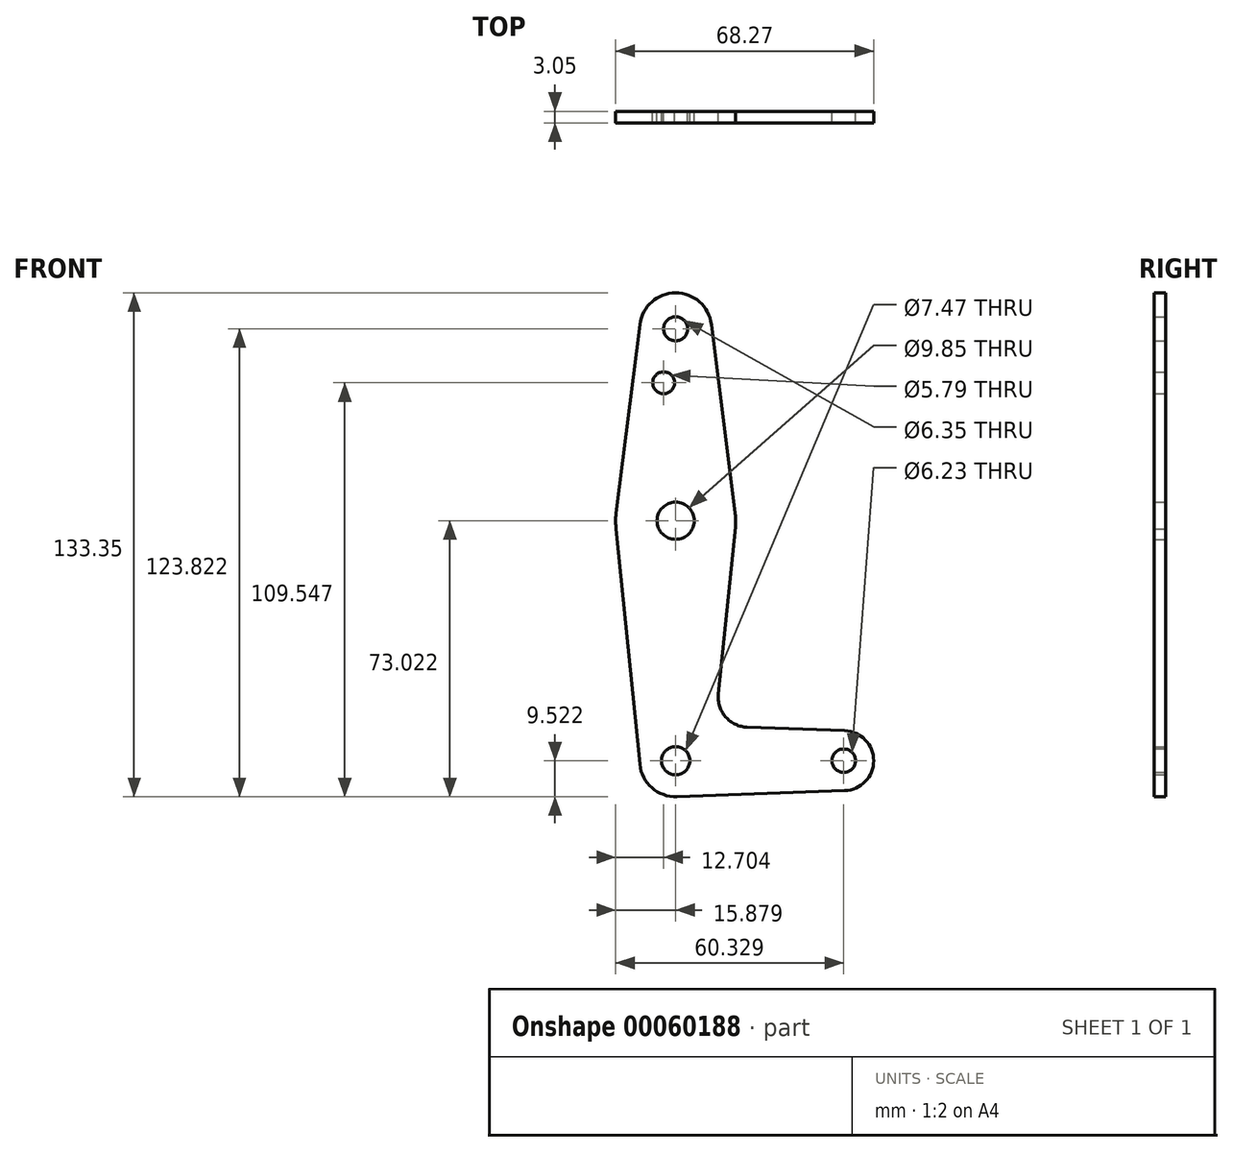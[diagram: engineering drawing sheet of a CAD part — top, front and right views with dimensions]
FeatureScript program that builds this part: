
annotation { "Feature Type Name" : "Feature", "Feature Type Description" : "" }
export const myFeature = defineFeature(function(context is Context, id is Id, definition is map)
    precondition{}
    {
        {
            var Q0;
            Q0=qCreatedBy(makeId("Front.planeOp"),FACE);
            var sketch = newSketch(context, id + "F0", { "sketchPlane" : qUnion([Q0])});
            skLineSegment(sketch, "E0", {"start": v(-32.87, 68.1) * mm, "end": v(-32.87, -46.2) * mm, "construction": true});
            skLineSegment(sketch, "E1", {"start": v(-32.87, -46.2) * mm, "end": v(11.58, -46.2) * mm, "construction": true});
            skCircle(sketch, "E2", {"center": v(-32.87, 68.1) * mm, "radius": 9.53 * mm});
            skCircle(sketch, "E3", {"center": v(-32.87, -46.2) * mm, "radius": 9.53 * mm});
            skCircle(sketch, "E4", {"center": v(11.58, -46.2) * mm, "radius": 7.94 * mm});
            skCircle(sketch, "E5", {"center": v(-32.87, 17.3) * mm, "radius": 15.88 * mm});
            skLineSegment(sketch, "E6", {"start": v(-23.42, 69.28) * mm, "end": v(-17.12, 19.28) * mm});
            skLineSegment(sketch, "E7", {"start": v(-42.32, 69.28) * mm, "end": v(-48.62, 19.28) * mm});
            skLineSegment(sketch, "E8", {"start": v(-48.6, 15.13) * mm, "end": v(-42.35, -47.16) * mm});
            skLineSegment(sketch, "E9", {"start": v(-32.53, -55.73) * mm, "end": v(11.86, -54.14) * mm});
            skLineSegment(sketch, "E10", {"start": v(11.86, -38.28) * mm, "end": v(-32.87, -36.68) * mm});
            skLineSegment(sketch, "E11", {"start": v(-23.35, -46.2) * mm, "end": v(-17.08, 15.7) * mm});
            skCircle(sketch, "E12", {"center": v(-32.87, 68.1) * mm, "radius": 3.18 * mm});
            skCircle(sketch, "E13", {"center": v(-32.87, 17.3) * mm, "radius": 4.92 * mm});
            skCircle(sketch, "E14", {"center": v(-32.87, -46.2) * mm, "radius": 3.74 * mm});
            skCircle(sketch, "E15", {"center": v(11.58, -46.2) * mm, "radius": 3.12 * mm});
            skPoint(sketch, "E16", {"position": v(-36.05, 53.82) * mm});
            skCircle(sketch, "E17", {"center": v(-36.05, 53.82) * mm, "radius": 2.9 * mm});
            skArc(sketch, "E18", {"start": v(-21.56, -28.6) * mm, "mid": v(-19.65, -34.63) * mm, "end": v(-13.94, -37.35) * mm});
            skSolve(sketch);
        }
        {
            var Q0;
            Q0=makeQuery(id+"F0.imprint","IMPRINT",FACE,{"disambiguationData":[TD([[makeQuery(id+"F0.imprint","IMPRINT",EDGE,{"derivedFrom":sQuery(id+"F0.wireOp",EDGE,"E12")}),-1.0]])]});
            var Q1;
            {var subQ1=sQuery(id+"F0.wireOp",EDGE,"E6");Q1=makeQuery(id+"F0.imprint","IMPRINT",FACE,{"disambiguationData":[TD([[makeQuery(id+"F0.imprint","IMPRINT",EDGE,{"derivedFrom":subQ1}),-1.0]])]});}
            var Q2;
            Q2=makeQuery(id+"F0.imprint","IMPRINT",FACE,{"disambiguationData":[TD([[makeQuery(id+"F0.imprint","IMPRINT",EDGE,{"derivedFrom":sQuery(id+"F0.wireOp",EDGE,"E13")}),-1.0]])]});
            var Q3;
            {var subQ0=sQuery(id+"F0.wireOp",EDGE,"E8");Q3=makeQuery(id+"F0.imprint","IMPRINT",FACE,{"disambiguationData":[TD([[makeQuery(id+"F0.imprint","IMPRINT",EDGE,{"derivedFrom":subQ0}),1.0]])]});}
            var Q4;
            Q4=makeQuery(id+"F0.imprint","IMPRINT",FACE,{"disambiguationData":[TD([[makeQuery(id+"F0.imprint","IMPRINT",EDGE,{"derivedFrom":sQuery(id+"F0.wireOp",EDGE,"E14")}),-1.0]])]});
            var Q5;
            {var subQ0=sQuery(id+"F0.wireOp",EDGE,"E11");var subQ1=sQuery(id+"F0.wireOp",EDGE,"E3");var subQ2=makeQuery(id+"F0.imprint","INTERSECT",VERTEX,{"derivedFrom":[subQ1,subQ0]});Q5=makeQuery(id+"F0.imprint","IMPRINT",FACE,{"disambiguationData":[TD([[makeQuery(id+"F0.imprint","IMPRINT",EDGE,{"disambiguationData":[TD([[subQ2,-1.0]])],"derivedFrom":subQ1}),-1.0]])]});}
            var Q6;
            {var subQ0=sQuery(id+"F0.wireOp",EDGE,"E18");Q6=makeQuery(id+"F0.imprint","IMPRINT",FACE,{"disambiguationData":[TD([[makeQuery(id+"F0.imprint","IMPRINT",EDGE,{"derivedFrom":subQ0}),-1.0]])]});}
            var Q7;
            {var subQ4=sQuery(id+"F0.wireOp",EDGE,"E9");Q7=makeQuery(id+"F0.imprint","IMPRINT",FACE,{"disambiguationData":[TD([[makeQuery(id+"F0.imprint","IMPRINT",EDGE,{"derivedFrom":subQ4}),1.0]])]});}
            var Q8;
            Q8=makeQuery(id+"F0.imprint","IMPRINT",FACE,{"disambiguationData":[TD([[makeQuery(id+"F0.imprint","IMPRINT",EDGE,{"derivedFrom":sQuery(id+"F0.wireOp",EDGE,"E15")}),-1.0]])]});
            extrude(context, id + "F1", {"entities" : qUnion([Q0, Q1, Q2, Q3, Q4, Q5, Q6, Q7, Q8]), "depth" : 3.05 * mm});
        }
    });
